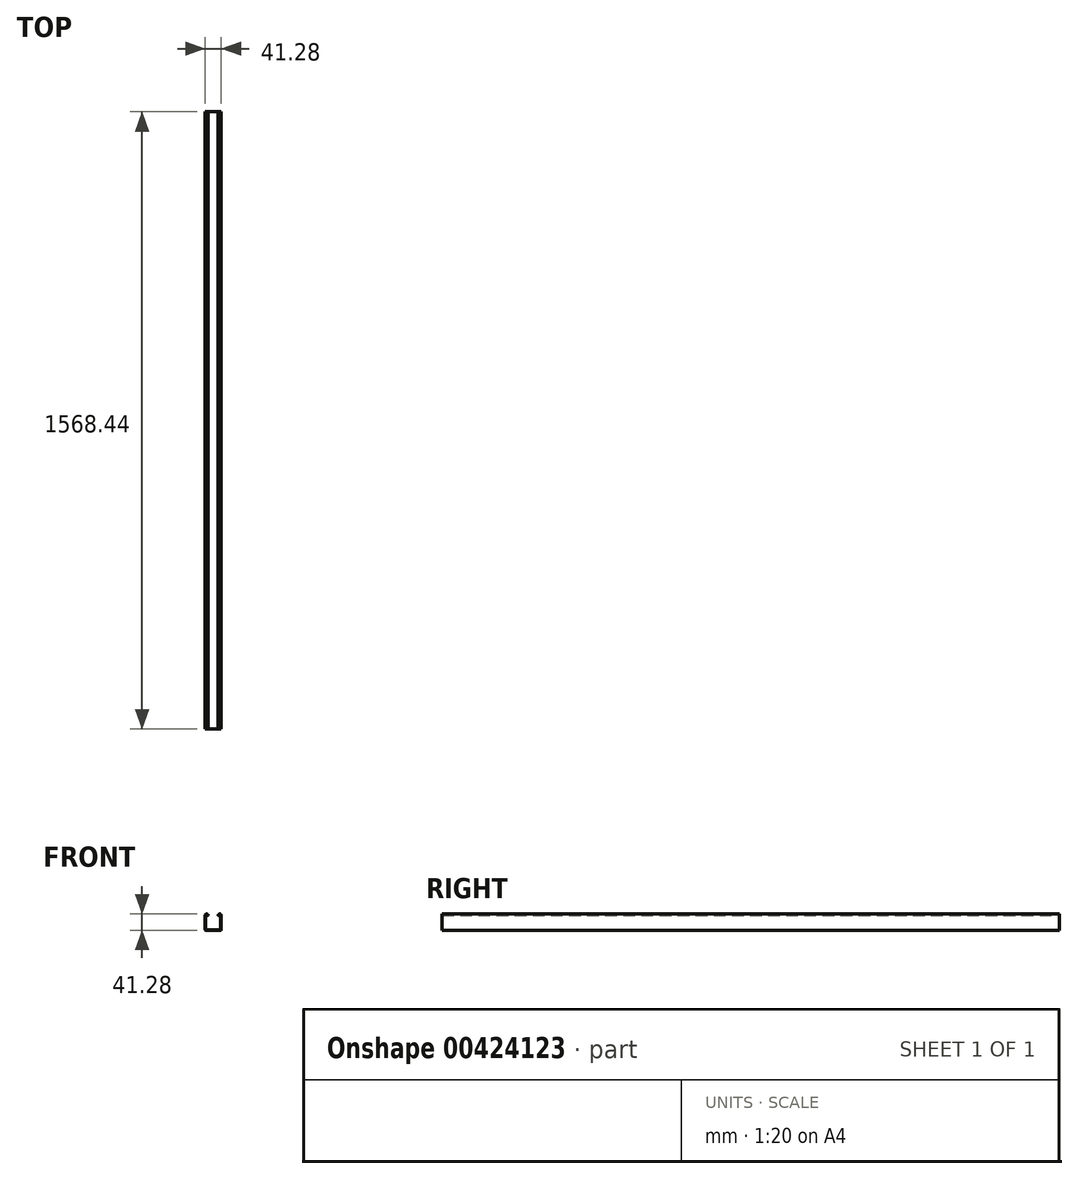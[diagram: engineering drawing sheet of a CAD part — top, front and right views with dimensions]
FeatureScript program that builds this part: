
annotation { "Feature Type Name" : "Feature", "Feature Type Description" : "" }
export const myFeature = defineFeature(function(context is Context, id is Id, definition is map)
    precondition{}
    {
        {
            var Q0;
            Q0=qCreatedBy(makeId("Front.planeOp"),FACE);
            var sketch = newSketch(context, id + "F0", { "sketchPlane" : qUnion([Q0])});
            skLineSegment(sketch, "E0.bottom", {"start": v(0, 0) * mm, "end": v(41.28, 0) * mm});
            skLineSegment(sketch, "E0.left", {"start": v(0, 0) * mm, "end": v(0, 37.31) * mm});
            skLineSegment(sketch, "E0.right", {"start": v(41.28, 0) * mm, "end": v(41.28, 37.31) * mm});
            skLineSegment(sketch, "E1.0", {"start": v(1.59, 1.59) * mm, "end": v(1.59, 37.31) * mm});
            skLineSegment(sketch, "E2.0", {"start": v(1.59, 1.59) * mm, "end": v(39.69, 1.59) * mm});
            skLineSegment(sketch, "E3.0", {"start": v(39.69, 1.59) * mm, "end": v(39.69, 37.31) * mm});
            skArc(sketch, "E4", {"start": v(7.92, 37.31) * mm, "mid": v(3.96, 41.28) * mm, "end": v(0, 37.31) * mm});
            skArc(sketch, "E5", {"start": v(6.34, 37.31) * mm, "mid": v(3.96, 39.69) * mm, "end": v(1.59, 37.31) * mm});
            skArc(sketch, "E6.MirrorC", {"start": v(33.35, 37.31) * mm, "mid": v(37.31, 41.28) * mm, "end": v(41.28, 37.31) * mm});
            skArc(sketch, "E7.MirrorC", {"start": v(34.94, 37.31) * mm, "mid": v(37.31, 39.69) * mm, "end": v(39.69, 37.31) * mm});
            skLineSegment(sketch, "E8.trimOffspring", {"start": v(6.34, 37.31) * mm, "end": v(7.92, 37.31) * mm});
            skLineSegment(sketch, "E9.trimOffspring", {"start": v(33.35, 37.31) * mm, "end": v(34.94, 37.31) * mm});
            skSolve(sketch);
        }
        {
            var Q0;
            Q0 = qSketchRegion(id + "F0", true);
            extrude(context, id + "F1", {"entities" : qUnion([Q0]), "endBound" : BoundingType.SYMMETRIC, "depth" : 1568.45 * mm});
        }
        {
            var Q0;
            Q0=makeQuery(id+"F1.opExtrude","SWEPT_EDGE",EDGE,{"disambiguationData":[OSD([sQuery(id+"F0.wireOp",EDGE,"E0.bottom"),sQuery(id+"F0.wireOp",EDGE,"E0.left")])]});
            var Q1;
            Q1=makeQuery(id+"F1.opExtrude","SWEPT_EDGE",EDGE,{"disambiguationData":[OSD([sQuery(id+"F0.wireOp",EDGE,"E0.bottom"),sQuery(id+"F0.wireOp",EDGE,"E0.right")])]});
            var Q2;
            Q2=makeQuery(id+"F1.opExtrude","SWEPT_EDGE",EDGE,{"disambiguationData":[OSD([sQuery(id+"F0.wireOp",EDGE,"E1.0"),sQuery(id+"F0.wireOp",EDGE,"E2.0")])]});
            var Q3;
            Q3=makeQuery(id+"F1.opExtrude","SWEPT_EDGE",EDGE,{"disambiguationData":[OSD([sQuery(id+"F0.wireOp",EDGE,"E2.0"),sQuery(id+"F0.wireOp",EDGE,"E3.0")])]});
            fillet(context, id + "F2", {"entities" : qUnion([Q0, Q1, Q2, Q3]), "radius" : 1.59 * mm, "tangentPropagation" : true, "allowEdgeOverflow" : false});
        }
        {
            var Q0;
            Q0=makeQuery(id+"F1.opExtrude","SWEPT_EDGE",EDGE,{"disambiguationData":[OSD([sQuery(id+"F0.wireOp",EDGE,"E5"),sQuery(id+"F0.wireOp",EDGE,"E8.trimOffspring")])]});
            var Q1;
            Q1=makeQuery(id+"F1.opExtrude","SWEPT_EDGE",EDGE,{"disambiguationData":[OSD([sQuery(id+"F0.wireOp",EDGE,"E4"),sQuery(id+"F0.wireOp",EDGE,"E8.trimOffspring")])]});
            var Q2;
            Q2=makeQuery(id+"F1.opExtrude","SWEPT_EDGE",EDGE,{"disambiguationData":[OSD([sQuery(id+"F0.wireOp",EDGE,"E6.MirrorC"),sQuery(id+"F0.wireOp",EDGE,"E9.trimOffspring")])]});
            var Q3;
            Q3=makeQuery(id+"F1.opExtrude","SWEPT_EDGE",EDGE,{"disambiguationData":[OSD([sQuery(id+"F0.wireOp",EDGE,"E7.MirrorC"),sQuery(id+"F0.wireOp",EDGE,"E9.trimOffspring")])]});
            fillet(context, id + "F3", {"entities" : qUnion([Q0, Q1, Q2, Q3]), "radius" : 0.64 * mm, "tangentPropagation" : true, "allowEdgeOverflow" : false});
        }
    });
